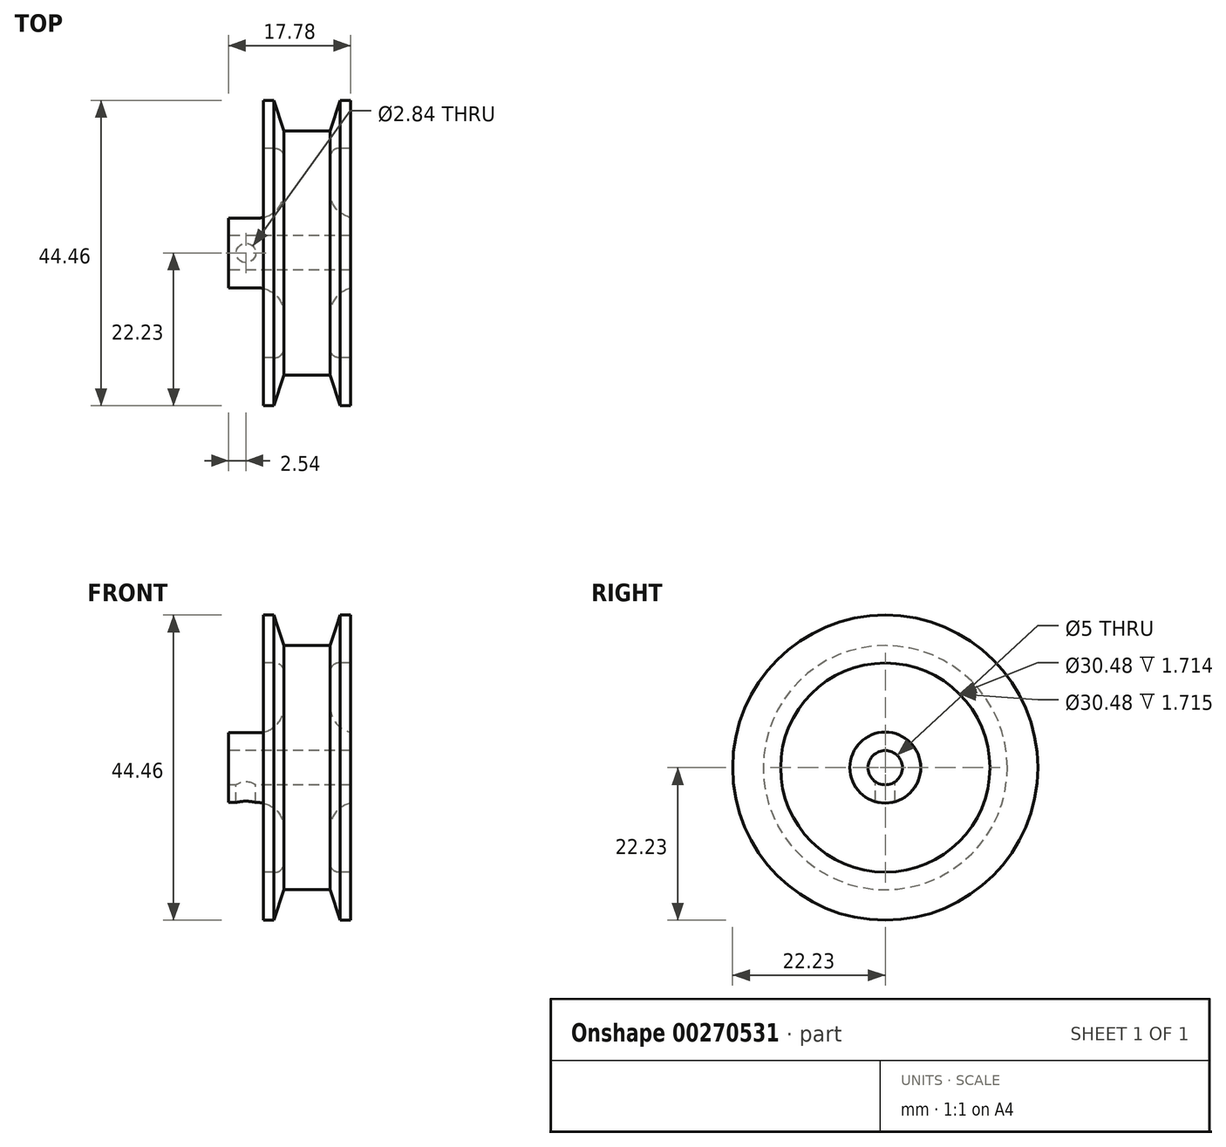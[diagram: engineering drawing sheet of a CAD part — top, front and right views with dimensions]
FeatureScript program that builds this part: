
annotation { "Feature Type Name" : "Feature", "Feature Type Description" : "" }
export const myFeature = defineFeature(function(context is Context, id is Id, definition is map)
    precondition{}
    {
        {
            var Q0;
            Q0=qCreatedBy(makeId("Front.planeOp"),FACE);
            var sketch = newSketch(context, id + "F0", { "sketchPlane" : qUnion([Q0])});
            skLineSegment(sketch, "E0", {"start": v(0, 0) * mm, "end": v(10.8, 0) * mm, "construction": true});
            skLineSegment(sketch, "E1", {"start": v(0, 22.23) * mm, "end": v(1.52, 22.23) * mm});
            skLineSegment(sketch, "E2", {"start": v(1.52, 22.23) * mm, "end": v(2.98, 17.78) * mm});
            skLineSegment(sketch, "E3", {"start": v(2.98, 17.78) * mm, "end": v(6.35, 17.78) * mm});
            skLineSegment(sketch, "E4", {"start": v(6.35, 17.78) * mm, "end": v(6.35, 0) * mm, "construction": true});
            skLineSegment(sketch, "E5", {"start": v(6.35, 2.5) * mm, "end": v(-5.08, 2.5) * mm});
            skLineSegment(sketch, "E6", {"start": v(-5.08, 2.5) * mm, "end": v(-5.08, 5.08) * mm});
            skLineSegment(sketch, "E7", {"start": v(-5.08, 5.08) * mm, "end": v(0, 5.08) * mm});
            skLineSegment(sketch, "E8.trimOffspring", {"start": v(0, 15.24) * mm, "end": v(0, 22.23) * mm});
            skLineSegment(sketch, "E9.MirrorCS", {"start": v(6.35, 2.5) * mm, "end": v(12.7, 2.5) * mm});
            skLineSegment(sketch, "E10.MirrorCS", {"start": v(12.7, 5.08) * mm, "end": v(12.7, 5.17) * mm});
            skLineSegment(sketch, "E11.MirrorCS", {"start": v(12.7, 22.23) * mm, "end": v(11.18, 22.23) * mm});
            skLineSegment(sketch, "E12.MirrorCS", {"start": v(11.18, 22.23) * mm, "end": v(9.72, 17.78) * mm});
            skLineSegment(sketch, "E13.MirrorCS", {"start": v(9.72, 17.78) * mm, "end": v(6.35, 17.78) * mm});
            skLineSegment(sketch, "E14", {"start": v(12.7, 5.08) * mm, "end": v(12.7, 2.5) * mm});
            skPoint(sketch, "E15.orphan", {"position": v(17.78, 2.5) * mm});
            skLineSegment(sketch, "E16", {"start": v(-0.83, 5.08) * mm, "end": v(0, 5.08) * mm});
            skLineSegment(sketch, "E17", {"start": v(2.98, 8.9) * mm, "end": v(2.98, 13.97) * mm});
            skLineSegment(sketch, "E18", {"start": v(1.71, 15.24) * mm, "end": v(0, 15.24) * mm});
            skPoint(sketch, "E19.visualSharp", {"position": v(2.98, 15.24) * mm});
            skArc(sketch, "E19.filletArc", {"start": v(2.98, 13.97) * mm, "mid": v(2.61, 14.87) * mm, "end": v(1.71, 15.24) * mm});
            skPoint(sketch, "E20.visualSharp", {"position": v(2.98, 5.08) * mm});
            skArc(sketch, "E20.filletArc", {"start": v(-0.83, 5.08) * mm, "mid": v(1.87, 6.2) * mm, "end": v(2.98, 8.9) * mm});
            skLineSegment(sketch, "E21.MirrorCS", {"start": v(10.99, 15.24) * mm, "end": v(12.7, 15.24) * mm});
            skArc(sketch, "E22.MirrorCS", {"start": v(9.72, 13.97) * mm, "mid": v(10.09, 14.87) * mm, "end": v(10.99, 15.24) * mm});
            skLineSegment(sketch, "E23.MirrorCS", {"start": v(9.72, 8.9) * mm, "end": v(9.72, 13.97) * mm});
            skArc(sketch, "E24.MirrorCS", {"start": v(12.7, 5.17) * mm, "mid": v(10.55, 6.5) * mm, "end": v(9.72, 8.9) * mm});
            skLineSegment(sketch, "E25.trimOffspring", {"start": v(12.7, 15.24) * mm, "end": v(12.7, 22.23) * mm});
            skPoint(sketch, "E26.orphan", {"position": v(13.53, 5.08) * mm});
            skSolve(sketch);
        }
        {
            var Q0;
            Q0 = qSketchRegion(id + "F0", true);
            var Q1;
            Q1=sQuery(id+"F0.wireOp",EDGE,"E0");
            revolve(context, id + "F1", {"entities" : qUnion([Q0]), "axis" : qUnion([Q1]), "revolveType" : RevolveType.FULL});
        }
        {
            var Q0;
            Q0=qCreatedBy(makeId("Top.planeOp"),FACE);
            var sketch = newSketch(context, id + "F2", { "sketchPlane" : qUnion([Q0])});
            skCircle(sketch, "E27", {"center": v(-2.54, 0) * mm, "radius": 1.42 * mm});
            skSolve(sketch);
        }
        {
            var Q0;
            Q0 = qSketchRegion(id + "F2", true);
            extrude(context, id + "F3", {"entities" : qUnion([Q0]), "operationType" : NewBodyOperationType.REMOVE, "oppositeDirection" : true, "depth" : 25.4 * mm});
        }
    });
